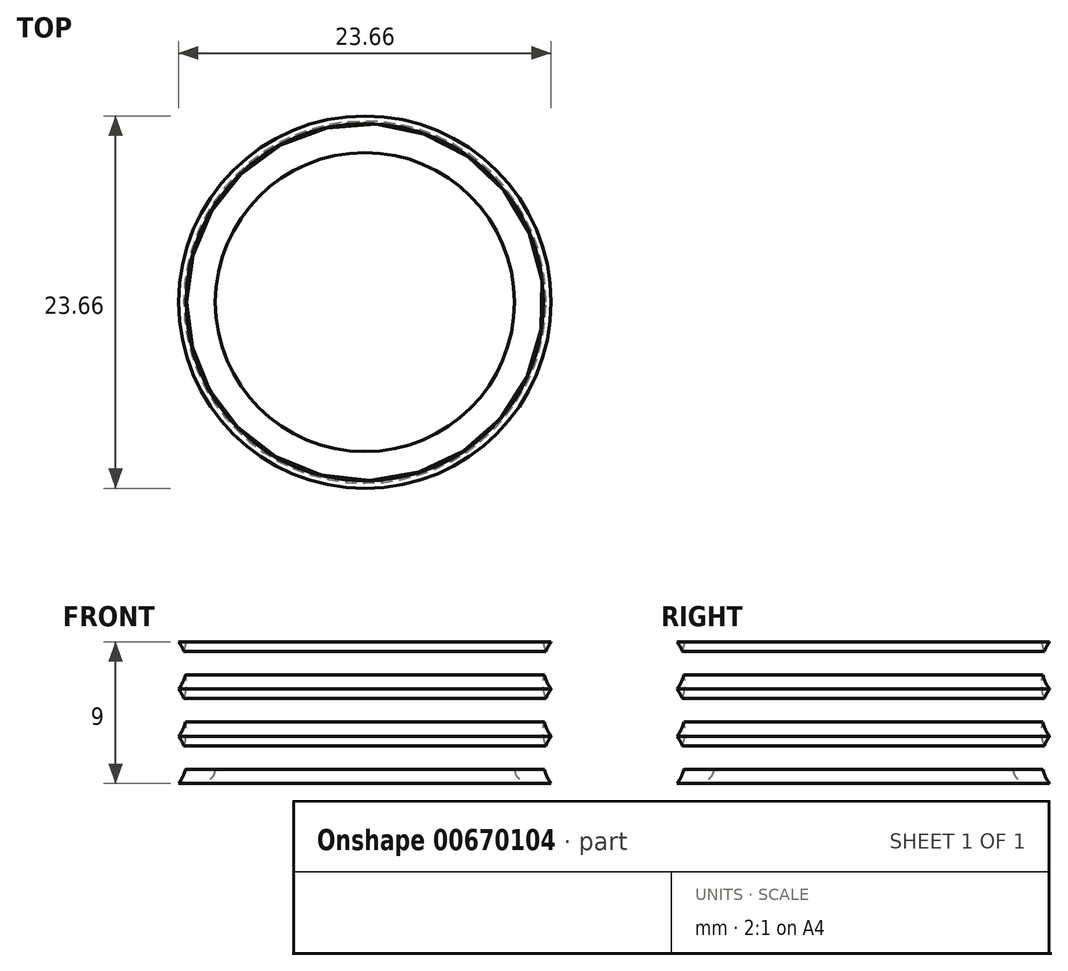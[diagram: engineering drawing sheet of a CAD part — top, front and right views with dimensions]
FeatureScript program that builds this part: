
annotation { "Feature Type Name" : "Feature", "Feature Type Description" : "" }
export const myFeature = defineFeature(function(context is Context, id is Id, definition is map)
    precondition{}
    {
        {
            var Q0;
            Q0=qCreatedBy(makeId("Front.planeOp"),FACE);
            var sketch = newSketch(context, id + "F0", { "sketchPlane" : qUnion([Q0])});
            skLineSegment(sketch, "E0", {"start": v(0, 0) * mm, "end": v(9.5, 0) * mm});
            skLineSegment(sketch, "E1", {"start": v(9.5, 1.5) * mm, "end": v(9.5, -1.5) * mm});
            skPoint(sketch, "E2", {"position": v(9.5, 0) * mm});
            skLineSegment(sketch, "E3", {"start": v(9.5, 1.5) * mm, "end": v(11.5, 1.5) * mm});
            skLineSegment(sketch, "E4", {"start": v(11.5, 1.5) * mm, "end": v(11.5, -1.5) * mm});
            skLineSegment(sketch, "E5", {"start": v(11.5, -1.5) * mm, "end": v(9.5, -1.5) * mm});
            skLineSegment(sketch, "E6", {"start": v(9.5, 0) * mm, "end": v(14.5, 0) * mm});
            skLineSegment(sketch, "E7", {"start": v(0, 0) * mm, "end": v(0, 24.34) * mm});
            skCircle(sketch, "E8", {"center": v(13.83, 2.4) * mm, "radius": 2.5 * mm});
            skCircle(sketch, "E9", {"center": v(13.83, -2.4) * mm, "radius": 2.5 * mm});
            skLineSegment(sketch, "E10", {"start": v(0, 3) * mm, "end": v(9.5, 3) * mm});
            skLineSegment(sketch, "E11", {"start": v(9.5, 4.5) * mm, "end": v(9.5, 1.5) * mm});
            skPoint(sketch, "E12", {"position": v(9.5, 3) * mm});
            skLineSegment(sketch, "E13", {"start": v(9.5, 4.5) * mm, "end": v(11.5, 4.5) * mm});
            skLineSegment(sketch, "E14", {"start": v(11.5, 4.5) * mm, "end": v(11.5, 1.5) * mm});
            skLineSegment(sketch, "E15", {"start": v(11.5, 1.5) * mm, "end": v(9.5, 1.5) * mm});
            skLineSegment(sketch, "E16", {"start": v(9.5, 3) * mm, "end": v(14.5, 3) * mm});
            skCircle(sketch, "E17", {"center": v(13.83, 5.4) * mm, "radius": 2.5 * mm});
            skCircle(sketch, "E18", {"center": v(13.83, 0.6) * mm, "radius": 2.5 * mm});
            skLineSegment(sketch, "E19", {"start": v(0, 6) * mm, "end": v(9.5, 6) * mm});
            skLineSegment(sketch, "E20", {"start": v(9.5, 7.5) * mm, "end": v(9.5, 4.5) * mm});
            skPoint(sketch, "E21", {"position": v(9.5, 6) * mm});
            skLineSegment(sketch, "E22", {"start": v(9.5, 7.5) * mm, "end": v(11.5, 7.5) * mm});
            skLineSegment(sketch, "E23", {"start": v(11.5, 7.5) * mm, "end": v(11.5, 4.5) * mm});
            skLineSegment(sketch, "E24", {"start": v(11.5, 4.5) * mm, "end": v(9.5, 4.5) * mm});
            skLineSegment(sketch, "E25", {"start": v(9.5, 6) * mm, "end": v(14.5, 6) * mm});
            skCircle(sketch, "E26", {"center": v(13.83, 8.4) * mm, "radius": 2.5 * mm});
            skCircle(sketch, "E27", {"center": v(13.83, 3.6) * mm, "radius": 2.5 * mm});
            skLineSegment(sketch, "E28", {"start": v(0, 9) * mm, "end": v(9.5, 9) * mm});
            skLineSegment(sketch, "E29", {"start": v(9.5, 10.5) * mm, "end": v(9.5, 7.5) * mm});
            skPoint(sketch, "E30", {"position": v(9.5, 9) * mm});
            skLineSegment(sketch, "E31", {"start": v(9.5, 10.5) * mm, "end": v(11.5, 10.5) * mm});
            skLineSegment(sketch, "E32", {"start": v(11.5, 10.5) * mm, "end": v(11.5, 7.5) * mm});
            skLineSegment(sketch, "E33", {"start": v(11.5, 7.5) * mm, "end": v(9.5, 7.5) * mm});
            skLineSegment(sketch, "E34", {"start": v(9.5, 9) * mm, "end": v(14.5, 9) * mm});
            skCircle(sketch, "E35", {"center": v(13.83, 11.4) * mm, "radius": 2.5 * mm});
            skCircle(sketch, "E36", {"center": v(13.83, 6.6) * mm, "radius": 2.5 * mm});
            skLineSegment(sketch, "E37", {"start": v(0, 12) * mm, "end": v(9.5, 12) * mm});
            skLineSegment(sketch, "E38", {"start": v(9.5, 13.5) * mm, "end": v(9.5, 10.5) * mm});
            skPoint(sketch, "E39", {"position": v(9.5, 12) * mm});
            skLineSegment(sketch, "E40", {"start": v(9.5, 13.5) * mm, "end": v(11.5, 13.5) * mm});
            skLineSegment(sketch, "E41", {"start": v(11.5, 13.5) * mm, "end": v(11.5, 10.5) * mm});
            skLineSegment(sketch, "E42", {"start": v(11.5, 10.5) * mm, "end": v(9.5, 10.5) * mm});
            skLineSegment(sketch, "E43", {"start": v(9.5, 12) * mm, "end": v(14.5, 12) * mm});
            skCircle(sketch, "E44", {"center": v(13.83, 14.4) * mm, "radius": 2.5 * mm});
            skCircle(sketch, "E45", {"center": v(13.83, 9.6) * mm, "radius": 2.5 * mm});
            skLineSegment(sketch, "E46", {"start": v(0, 15) * mm, "end": v(9.5, 15) * mm});
            skLineSegment(sketch, "E47", {"start": v(9.5, 16.5) * mm, "end": v(9.5, 13.5) * mm});
            skPoint(sketch, "E48", {"position": v(9.5, 15) * mm});
            skLineSegment(sketch, "E49", {"start": v(9.5, 16.5) * mm, "end": v(11.5, 16.5) * mm});
            skLineSegment(sketch, "E50", {"start": v(11.5, 16.5) * mm, "end": v(11.5, 13.5) * mm});
            skLineSegment(sketch, "E51", {"start": v(11.5, 13.5) * mm, "end": v(9.5, 13.5) * mm});
            skLineSegment(sketch, "E52", {"start": v(9.5, 15) * mm, "end": v(14.5, 15) * mm});
            skCircle(sketch, "E53", {"center": v(13.83, 17.4) * mm, "radius": 2.5 * mm});
            skCircle(sketch, "E54", {"center": v(13.83, 12.6) * mm, "radius": 2.5 * mm});
            skLineSegment(sketch, "E55", {"start": v(11.83, 2.1) * mm, "end": v(9.5, 2.1) * mm});
            skLineSegment(sketch, "E56", {"start": v(11.83, 11.1) * mm, "end": v(9.5, 11.1) * mm});
            skSolve(sketch);
        }
        {
            var Q0;
            {var subQ3=sQuery(id+"F0.wireOp",EDGE,"E24");Q0=makeQuery(id+"F0.imprint","IMPRINT",FACE,{"disambiguationData":[TD([[makeQuery(id+"F0.imprint","IMPRINT",EDGE,{"derivedFrom":subQ3}),1.0]])]});}
            var Q1;
            {var subQ0=sQuery(id+"F0.wireOp",EDGE,"E24");Q1=makeQuery(id+"F0.imprint","IMPRINT",FACE,{"disambiguationData":[TD([[makeQuery(id+"F0.imprint","IMPRINT",EDGE,{"derivedFrom":subQ0}),-1.0]])]});}
            var Q2;
            {var subQ3=sQuery(id+"F0.wireOp",EDGE,"E33");Q2=makeQuery(id+"F0.imprint","IMPRINT",FACE,{"disambiguationData":[TD([[makeQuery(id+"F0.imprint","IMPRINT",EDGE,{"derivedFrom":subQ3}),1.0]])]});}
            var Q3;
            {var subQ1=sQuery(id+"F0.wireOp",EDGE,"E32");var subQ3=sQuery(id+"F0.wireOp",EDGE,"E45");var subQ4=makeQuery(id+"F0.imprint","INTERSECT",VERTEX,{"derivedFrom":[subQ1,subQ3]});Q3=makeQuery(id+"F0.imprint","IMPRINT",FACE,{"disambiguationData":[TD([[makeQuery(id+"F0.imprint","IMPRINT",EDGE,{"disambiguationData":[TD([[subQ4,-1.0]])],"derivedFrom":subQ3}),-1.0]])]});}
            var Q4;
            {var subQ0=sQuery(id+"F0.wireOp",EDGE,"E23");var subQ3=sQuery(id+"F0.wireOp",EDGE,"E36");var subQ5=makeQuery(id+"F0.imprint","INTERSECT",VERTEX,{"derivedFrom":[subQ0,subQ3]});Q4=makeQuery(id+"F0.imprint","IMPRINT",FACE,{"disambiguationData":[TD([[makeQuery(id+"F0.imprint","IMPRINT",EDGE,{"disambiguationData":[TD([[subQ5,1.0]])],"derivedFrom":subQ3}),-1.0]])]});}
            var Q5;
            {var subQ1=sQuery(id+"F0.wireOp",EDGE,"E23");var subQ3=sQuery(id+"F0.wireOp",EDGE,"E36");var subQ4=makeQuery(id+"F0.imprint","INTERSECT",VERTEX,{"derivedFrom":[subQ1,subQ3]});Q5=makeQuery(id+"F0.imprint","IMPRINT",FACE,{"disambiguationData":[TD([[makeQuery(id+"F0.imprint","IMPRINT",EDGE,{"disambiguationData":[TD([[subQ4,-1.0]])],"derivedFrom":subQ3}),-1.0]])]});}
            var Q6;
            {var subQ0=sQuery(id+"F0.wireOp",EDGE,"E14");var subQ3=sQuery(id+"F0.wireOp",EDGE,"E27");var subQ5=makeQuery(id+"F0.imprint","INTERSECT",VERTEX,{"derivedFrom":[subQ0,subQ3]});Q6=makeQuery(id+"F0.imprint","IMPRINT",FACE,{"disambiguationData":[TD([[makeQuery(id+"F0.imprint","IMPRINT",EDGE,{"disambiguationData":[TD([[subQ5,1.0]])],"derivedFrom":subQ3}),-1.0]])]});}
            var Q7;
            {var subQ1=sQuery(id+"F0.wireOp",EDGE,"E14");var subQ3=sQuery(id+"F0.wireOp",EDGE,"E27");var subQ4=makeQuery(id+"F0.imprint","INTERSECT",VERTEX,{"derivedFrom":[subQ1,subQ3]});Q7=makeQuery(id+"F0.imprint","IMPRINT",FACE,{"disambiguationData":[TD([[makeQuery(id+"F0.imprint","IMPRINT",EDGE,{"disambiguationData":[TD([[subQ4,-1.0]])],"derivedFrom":subQ3}),-1.0]])]});}
            var Q8;
            {var subQ0=sQuery(id+"F0.wireOp",EDGE,"E33");Q8=makeQuery(id+"F0.imprint","IMPRINT",FACE,{"disambiguationData":[TD([[makeQuery(id+"F0.imprint","IMPRINT",EDGE,{"derivedFrom":subQ0}),-1.0]])]});}
            var Q9;
            {var subQ0=sQuery(id+"F0.wireOp",EDGE,"E32");var subQ3=sQuery(id+"F0.wireOp",EDGE,"E45");var subQ5=makeQuery(id+"F0.imprint","INTERSECT",VERTEX,{"derivedFrom":[subQ0,subQ3]});Q9=makeQuery(id+"F0.imprint","IMPRINT",FACE,{"disambiguationData":[TD([[makeQuery(id+"F0.imprint","IMPRINT",EDGE,{"disambiguationData":[TD([[subQ5,1.0]])],"derivedFrom":subQ3}),-1.0]])]});}
            var Q10;
            {var subQ3=sQuery(id+"F0.wireOp",EDGE,"E42");Q10=makeQuery(id+"F0.imprint","IMPRINT",FACE,{"disambiguationData":[TD([[makeQuery(id+"F0.imprint","IMPRINT",EDGE,{"derivedFrom":subQ3}),1.0]])]});}
            var Q11;
            {var subQ0=sQuery(id+"F0.wireOp",EDGE,"E55");var subQ5=sQuery(id+"F0.wireOp",EDGE,"E11");var subQ6=makeQuery(id+"F0.imprint","INTERSECT",VERTEX,{"derivedFrom":[subQ5,subQ0]});Q11=makeQuery(id+"F0.imprint","IMPRINT",FACE,{"disambiguationData":[TD([[makeQuery(id+"F0.imprint","IMPRINT",EDGE,{"disambiguationData":[TD([[subQ6,1.0]])],"derivedFrom":subQ0}),-1.0]])]});}
            var Q12;
            {var subQ0=sQuery(id+"F0.wireOp",EDGE,"E42");Q12=makeQuery(id+"F0.imprint","IMPRINT",FACE,{"disambiguationData":[TD([[makeQuery(id+"F0.imprint","IMPRINT",EDGE,{"derivedFrom":subQ0}),-1.0]])]});}
            var Q13;
            {var subQ1=sQuery(id+"F0.wireOp",EDGE,"E35");var subQ3=sQuery(id+"F0.wireOp",EDGE,"E56");var subQ4=makeQuery(id+"F0.imprint","INTERSECT",VERTEX,{"derivedFrom":[subQ1,subQ3]});Q13=makeQuery(id+"F0.imprint","IMPRINT",FACE,{"disambiguationData":[TD([[makeQuery(id+"F0.imprint","IMPRINT",EDGE,{"disambiguationData":[TD([[subQ4,1.0]])],"derivedFrom":subQ3}),1.0]])]});}
            var Q14;
            {var subQ1=sQuery(id+"F0.wireOp",EDGE,"E41");var subQ3=sQuery(id+"F0.wireOp",EDGE,"E56");var subQ4=makeQuery(id+"F0.imprint","INTERSECT",VERTEX,{"derivedFrom":[subQ1,subQ3]});Q14=makeQuery(id+"F0.imprint","IMPRINT",FACE,{"disambiguationData":[TD([[makeQuery(id+"F0.imprint","IMPRINT",EDGE,{"disambiguationData":[TD([[subQ4,1.0]])],"derivedFrom":subQ3}),1.0]])]});}
            var Q15;
            Q15=sQuery(id+"F0.wireOp",EDGE,"E7");
            revolve(context, id + "F1", {"entities" : qUnion([Q0, Q1, Q2, Q3, Q4, Q5, Q6, Q7, Q8, Q9, Q10, Q11, Q12, Q13, Q14]), "axis" : qUnion([Q15]), "revolveType" : RevolveType.FULL});
        }
        {
            var Q0;
            Q0=makeQuery(id+"F1.opRevolve","SWEPT_EDGE",EDGE,{"disambiguationData":[OSD([sQuery(id+"F0.wireOp",EDGE,"E38"),sQuery(id+"F0.wireOp",EDGE,"E56")])]});
            var Q1;
            Q1=makeQuery(id+"F1.opRevolve","SWEPT_EDGE",EDGE,{"disambiguationData":[OSD([sQuery(id+"F0.wireOp",EDGE,"E11"),sQuery(id+"F0.wireOp",EDGE,"E55")])]});
            fillet(context, id + "F2", {"entities" : qUnion([Q0, Q1]), "radius" : 1 * mm, "tangentPropagation" : true, "allowEdgeOverflow" : false});
        }
    });
